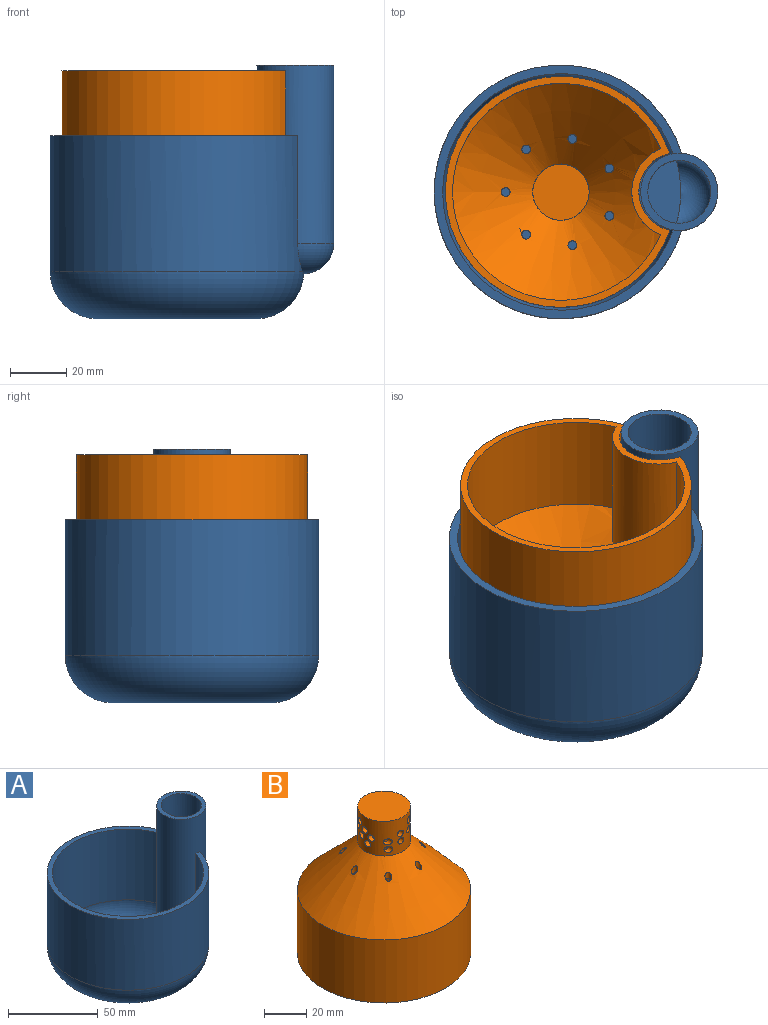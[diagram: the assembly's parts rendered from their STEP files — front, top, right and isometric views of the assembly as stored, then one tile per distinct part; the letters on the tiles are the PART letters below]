
ASSEMBLY  parts=2 mates=1
PART A: 17 faces, bbox 104.4x97.5x90 mm
  f0: cylinder r=45mm len=90mm, axis (0,0,-1), area 12305.2mm2, adj f4,f8,f9,f16
  f1: plane 27.36x27.36mm, normal (0,0,1), area 195.2mm2, adj f8,f14
  f2: cylinder r=42mm len=84mm, axis (0,0,-1), area 11371.6mm2, adj f6,f8,f16
  f3: plane 56.2x56.2mm, normal (0,0,-1), area 2480.7mm2, adj f4
  f4: torus R=28.1mm, axis (0,0,1), area 6475.3mm2, adj f0,f3,f9
  f5: plane 56.2x56.2mm, normal (0,0,1), area 2480.7mm2, adj f6
  f6: torus R=28.1mm, axis (0,0,1), area 5044mm2, adj f2,f5,f7,f8
  f7: plane 26.98x13.65mm, normal (0,0,-1), area 272.7mm2, adj f6,f8
  f8: cylinder r=13.68mm len=74mm, axis (0,0,1), area 5606.8mm2, adj f0,f1,f2,f6,f7,f9,f16
  f9: torus R=2.81mm, axis (0,0,1), area 455.8mm2, adj f0,f4,f8
  f10: plane 22.32x11.73mm, normal (0,0,1), area 196.4mm2, adj f11,f12,f13,f14
  f11: cylinder r=42.5mm len=8.36mm, axis (0,0,-1), area 15.2mm2, adj f10,f14,f15
  f12: cylinder r=42.5mm len=8.36mm, axis (0,0,-1), area 15.2mm2, adj f10,f14,f15
  f13: cylinder r=42.5mm len=5.57mm, axis (0,0,-1), area 0mm2, adj f10,f15
  f14: cylinder r=11.18mm len=71.5mm, axis (0,0,1), area 4711.9mm2, adj f1,f10,f11,f12,f15
  f15: torus R=2.81mm, axis (0,0,1), area 355.4mm2, adj f11,f12,f13,f14
  f16: plane 90x87.88mm, normal (0,0,1), area 736.8mm2, adj f0,f2,f8
PART B: 42 faces, bbox 82x82x85 mm
  f0: cylinder r=13.97mm len=49.86mm, axis (0,0,1), area 1684.4mm2, adj f1,f4,f41
  f1: cylinder r=41mm len=82mm, axis (0,0,1), area 8386.7mm2, adj f0,f4,f41
  f2: cylinder r=16.47mm len=48.82mm, axis (0,0,1), area 1702.7mm2, adj f3,f5,f41
  f3: cylinder r=38.5mm len=77mm, axis (0,0,1), area 7468mm2, adj f2,f5,f41
  f4: cone r=12.5mm half-angle=45deg, axis (0,0,-1), area 6321mm2, adj f0,f1,f6,f34,f35,f36,f37,f38
  f5: cone r=10.73mm half-angle=45deg, axis (0,0,-1), area 5657.4mm2, adj f2,f3,f8,f34,f35,f36,f37,f38
  f6: cylinder r=12.5mm len=25mm, axis (0,0,-1), area 1327.6mm2, adj f4,f7,f10,f11,f12,f13,f14,f15
  f7: plane 25x25mm, normal (0,0,1), area 490.9mm2, adj f6
  f8: cylinder r=10mm len=20mm, axis (0,0,-1), area 908.5mm2, adj f5,f9,f10,f11,f12,f13,f14,f15
  f9: plane 20x20mm, normal (0,0,-1), area 314.2mm2, adj f8
  f10: cylinder r=1.73mm len=6.91mm, axis (0,-1,0), area 37.1mm2, adj f6,f8,f25
  f11: cylinder r=1.73mm len=6.74mm, axis (0,-1,0), area 35.8mm2, adj f6,f8,f23,f24
  f12: cylinder r=1.73mm len=3.45mm, axis (0,-1,0), area 27.2mm2, adj f6,f8
  f13: cylinder r=1.73mm len=3.45mm, axis (0,-1,0), area 27.5mm2, adj f6,f8
  f14: cylinder r=1.73mm len=5.66mm, axis (0,-1,0), area 38mm2, adj f6,f8
  f15: cylinder r=1.73mm len=5.66mm, axis (0,-1,0), area 38mm2, adj f6,f8
  f16: cylinder r=1.73mm len=3.45mm, axis (0,-1,0), area 30.6mm2, adj f6,f8
  f17: cylinder r=1.73mm len=3.45mm, axis (0,-1,0), area 30.6mm2, adj f6,f8
  f18: cylinder r=1.73mm len=3.45mm, axis (0,-1,0), area 27.8mm2, adj f6,f8
  f19: cylinder r=1.73mm len=3.45mm, axis (0,-1,0), area 27.8mm2, adj f6,f8
  f20: cylinder r=1.73mm len=3.45mm, axis (0,-1,0), area 30mm2, adj f6,f8
  f21: cylinder r=1.73mm len=3.92mm, axis (0,-1,0), area 34.7mm2, adj f6,f8,f22
  f22: cylinder r=1.73mm len=5.91mm, axis (1,0,0), area 34.1mm2, adj f6,f8,f21
  f23: cylinder r=1.73mm len=3.45mm, axis (1,0,0), area 31.8mm2, adj f6,f8,f11
  f24: cylinder r=1.73mm len=6.03mm, axis (1,0,0), area 33.2mm2, adj f6,f8,f11
  f25: cylinder r=1.73mm len=3.78mm, axis (1,0,0), area 28.6mm2, adj f6,f8,f10
  f26: cylinder r=1.73mm len=3.45mm, axis (1,0,0), area 28.4mm2, adj f6,f8
  f27: cylinder r=1.73mm len=3.45mm, axis (1,0,0), area 28mm2, adj f6,f8
  f28: cylinder r=1.73mm len=3.45mm, axis (1,0,0), area 27.8mm2, adj f6,f8
  f29: cylinder r=1.73mm len=3.45mm, axis (1,0,0), area 27.1mm2, adj f6,f8
  f30: cylinder r=1.73mm len=3.45mm, axis (1,0,0), area 29.8mm2, adj f6,f8
  f31: cylinder r=1.73mm len=3.45mm, axis (1,0,0), area 29.8mm2, adj f6,f8
  f32: cylinder r=1.73mm len=3.45mm, axis (1,0,0), area 27.2mm2, adj f6,f8
  f33: cylinder r=1.73mm len=3.45mm, axis (1,0,0), area 27.1mm2, adj f6,f8
  f34: cylinder r=1.55mm len=6.64mm, axis (0,0,-1), area 34.2mm2, adj f4,f5
  f35: cylinder r=1.55mm len=6.64mm, axis (0,0,-1), area 34.3mm2, adj f4,f5
  f36: cylinder r=1.55mm len=6.64mm, axis (0,0,-1), area 34.8mm2, adj f4,f5
  f37: cylinder r=1.55mm len=6.64mm, axis (0,0,-1), area 34.5mm2, adj f4,f5
  f38: cylinder r=1.55mm len=6.64mm, axis (0,0,-1), area 34.3mm2, adj f4,f5
  f39: cylinder r=1.55mm len=6.64mm, axis (0,0,-1), area 34.5mm2, adj f4,f5
  f40: cylinder r=1.55mm len=6.64mm, axis (0,0,-1), area 35.1mm2, adj f4,f5
  f41: plane 82x79.66mm, normal (0,0,-1), area 646.4mm2, adj f0,f1,f2,f3
PLACE A t=(-45.35,-21.13,0)mm
PLACE B rot(axis=(1,0,0),180deg) t=(-17.51,-21.13,53)mm
MATE fastened B.f4 <-> A.f0  axis (0,0,-1) through (-45.35,-21.13,3)mm
